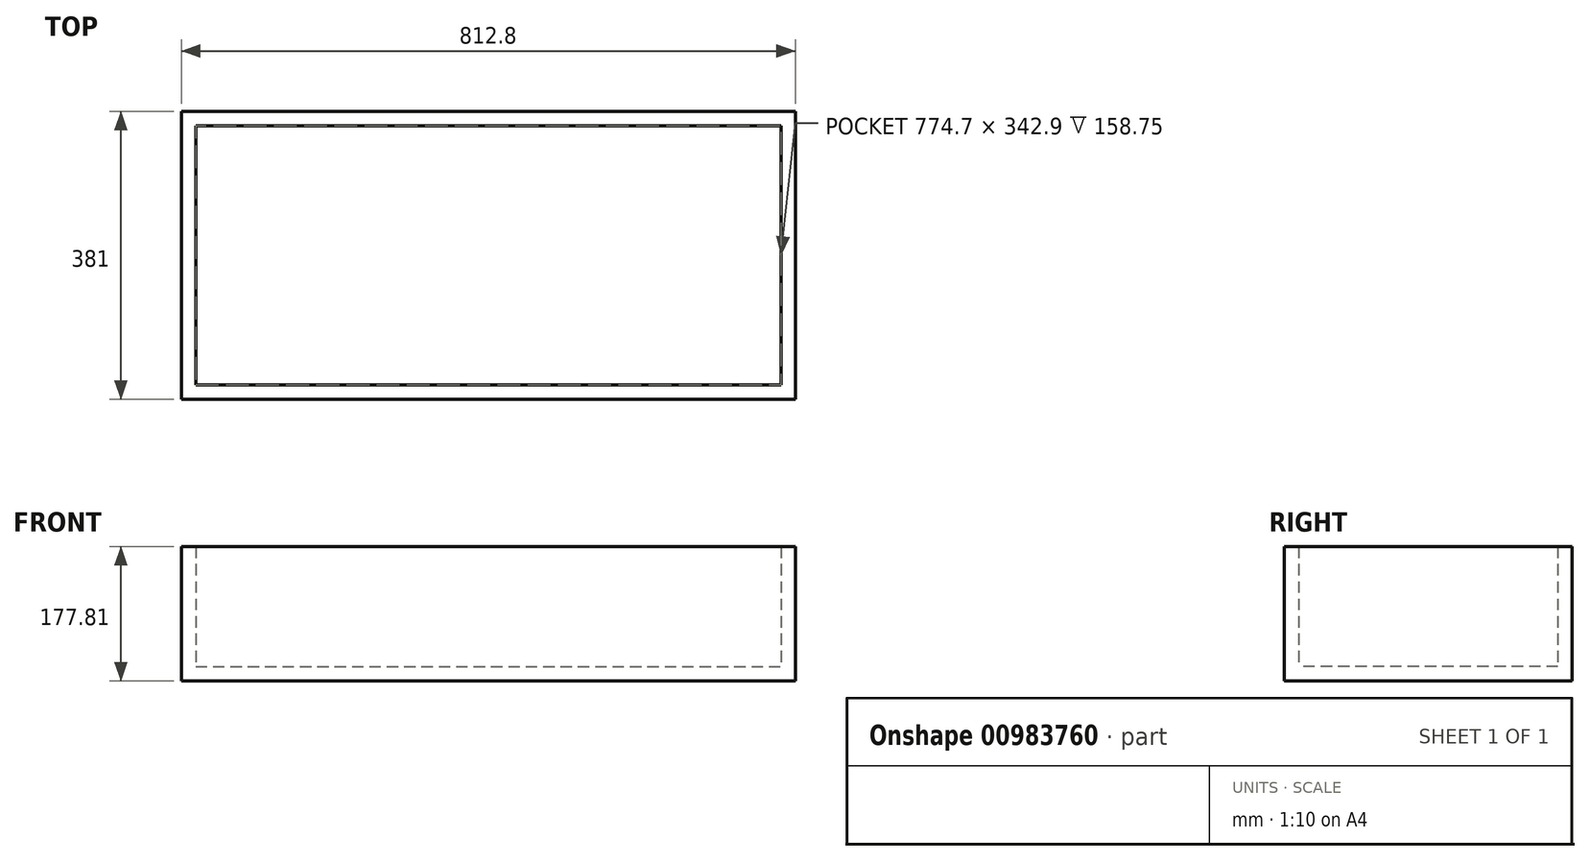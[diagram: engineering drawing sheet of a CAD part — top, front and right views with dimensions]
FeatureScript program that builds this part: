
annotation { "Feature Type Name" : "Feature", "Feature Type Description" : "" }
export const myFeature = defineFeature(function(context is Context, id is Id, definition is map)
    precondition{}
    {
        {
            var Q0;
            Q0=qCreatedBy(makeId("Front.planeOp"),FACE);
            var sketch = newSketch(context, id + "F0", { "sketchPlane" : qUnion([Q0])});
            skLineSegment(sketch, "E0.bottom", {"start": v(-406.4, 9.53) * mm, "end": v(406.4, 9.53) * mm});
            skLineSegment(sketch, "E0.top", {"start": v(-406.4, -9.52) * mm, "end": v(406.4, -9.52) * mm});
            skLineSegment(sketch, "E0.left", {"start": v(-406.4, 9.53) * mm, "end": v(-406.4, -9.52) * mm});
            skLineSegment(sketch, "E0.right", {"start": v(406.4, 9.53) * mm, "end": v(406.4, -9.52) * mm});
            skPoint(sketch, "E0.middle", {"position": v(0, 0) * mm});
            skSolve(sketch);
        }
        {
            var Q0;
            Q0=makeQuery(id+"F0.imprint","IMPRINT",FACE,{"disambiguationData":[TD([[makeQuery(id+"F0.imprint","IMPRINT",EDGE,{"derivedFrom":sQuery(id+"F0.wireOp",EDGE,"E0.bottom")}),-1.0]])]});
            extrude(context, id + "F1", {"entities" : qUnion([Q0]), "depth" : 381 * mm, "offsetDistance" : 25.4 * mm});
        }
        {
            var Q0;
            Q0=makeQuery(id+"F1.opExtrude","SWEPT_FACE",FACE,{"disambiguationData":[OSD([sQuery(id+"F0.wireOp",EDGE,"E0.bottom")])]});
            var sketch = newSketch(context, id + "F2", { "sketchPlane" : qUnion([Q0])});
            skLineSegment(sketch, "E1.bottom", {"start": v(-406.4, 0) * mm, "end": v(-387.35, 0) * mm});
            skLineSegment(sketch, "E1.top", {"start": v(-406.4, -361.95) * mm, "end": v(-387.35, -361.95) * mm});
            skLineSegment(sketch, "E1.left", {"start": v(-406.4, 0) * mm, "end": v(-406.4, -361.95) * mm});
            skLineSegment(sketch, "E1.right", {"start": v(-387.35, 0) * mm, "end": v(-387.35, -361.95) * mm});
            skSolve(sketch);
        }
        {
            var Q0;
            Q0=makeQuery(id+"F2.imprint","IMPRINT",FACE,{"disambiguationData":[TD([[makeQuery(id+"F2.imprint","IMPRINT",EDGE,{"derivedFrom":sQuery(id+"F2.wireOp",EDGE,"E1.bottom")}),-1.0]])]});
            extrude(context, id + "F3", {"entities" : qUnion([Q0]), "operationType" : NewBodyOperationType.ADD, "depth" : 158.75 * mm, "offsetDistance" : 25.4 * mm});
        }
        {
            var Q0;
            Q0=makeQuery(id+"F1.opExtrude","SWEPT_BODY",BODY,{"disambiguationData":[OSD([sQuery(id+"F0.wireOp",EDGE,"E0.bottom"),sQuery(id+"F0.wireOp",EDGE,"E0.top"),sQuery(id+"F0.wireOp",EDGE,"E0.left"),sQuery(id+"F0.wireOp",EDGE,"E0.right")])]});
            var Q1;
            Q1=qCreatedBy(makeId("Right.planeOp"),FACE);
            mirror(context, id + "F4", {"operationType" : NewBodyOperationType.ADD, "entities" : qUnion([Q0]), "mirrorPlane" : qUnion([Q1])});
        }
        {
            var Q0;
            Q0=makeQuery(id+"F1.opExtrude","SWEPT_FACE",FACE,{"disambiguationData":[OSD([sQuery(id+"F0.wireOp",EDGE,"E0.bottom")])]});
            var sketch = newSketch(context, id + "F5", { "sketchPlane" : qUnion([Q0])});
            skLineSegment(sketch, "E2.bottom", {"start": v(-387.35, 0) * mm, "end": v(387.35, 0) * mm});
            skLineSegment(sketch, "E2.top", {"start": v(-387.35, -19.05) * mm, "end": v(387.35, -19.05) * mm});
            skLineSegment(sketch, "E2.left", {"start": v(-387.35, 0) * mm, "end": v(-387.35, -19.05) * mm});
            skLineSegment(sketch, "E2.right", {"start": v(387.35, 0) * mm, "end": v(387.35, -19.05) * mm});
            skLineSegment(sketch, "E3.bottom", {"start": v(-406.4, -381) * mm, "end": v(406.4, -381) * mm});
            skLineSegment(sketch, "E3.top", {"start": v(-406.4, -361.95) * mm, "end": v(406.4, -361.95) * mm});
            skLineSegment(sketch, "E3.left", {"start": v(-406.4, -381) * mm, "end": v(-406.4, -361.95) * mm});
            skLineSegment(sketch, "E3.right", {"start": v(406.4, -381) * mm, "end": v(406.4, -361.95) * mm});
            skSolve(sketch);
        }
        {
            var Q0;
            Q0=makeQuery(id+"F5.imprint","IMPRINT",FACE,{"disambiguationData":[TD([[makeQuery(id+"F5.imprint","IMPRINT",EDGE,{"derivedFrom":sQuery(id+"F5.wireOp",EDGE,"E2.bottom")}),-1.0]])]});
            var Q1;
            Q1=makeQuery(id+"F5.imprint","IMPRINT",FACE,{"disambiguationData":[TD([[makeQuery(id+"F5.imprint","IMPRINT",EDGE,{"derivedFrom":sQuery(id+"F5.wireOp",EDGE,"E3.bottom")}),1.0]])]});
            var Q2;
            Q2=makeQuery(id+"F3.opExtrude","CAP_FACE",FACE,{"disambiguationData":[OSD([sQuery(id+"F2.wireOp",EDGE,"E1.bottom"),sQuery(id+"F2.wireOp",EDGE,"E1.top"),sQuery(id+"F2.wireOp",EDGE,"E1.left"),sQuery(id+"F2.wireOp",EDGE,"E1.right")])],"isStart":false});
            extrude(context, id + "F6", {"entities" : qUnion([Q0, Q1]), "operationType" : NewBodyOperationType.ADD, "endBound" : BoundingType.UP_TO_SURFACE, "depth" : 25.4 * mm, "endBoundEntityFace" : qUnion([Q2]), "offsetDistance" : 25.4 * mm});
        }
    });
